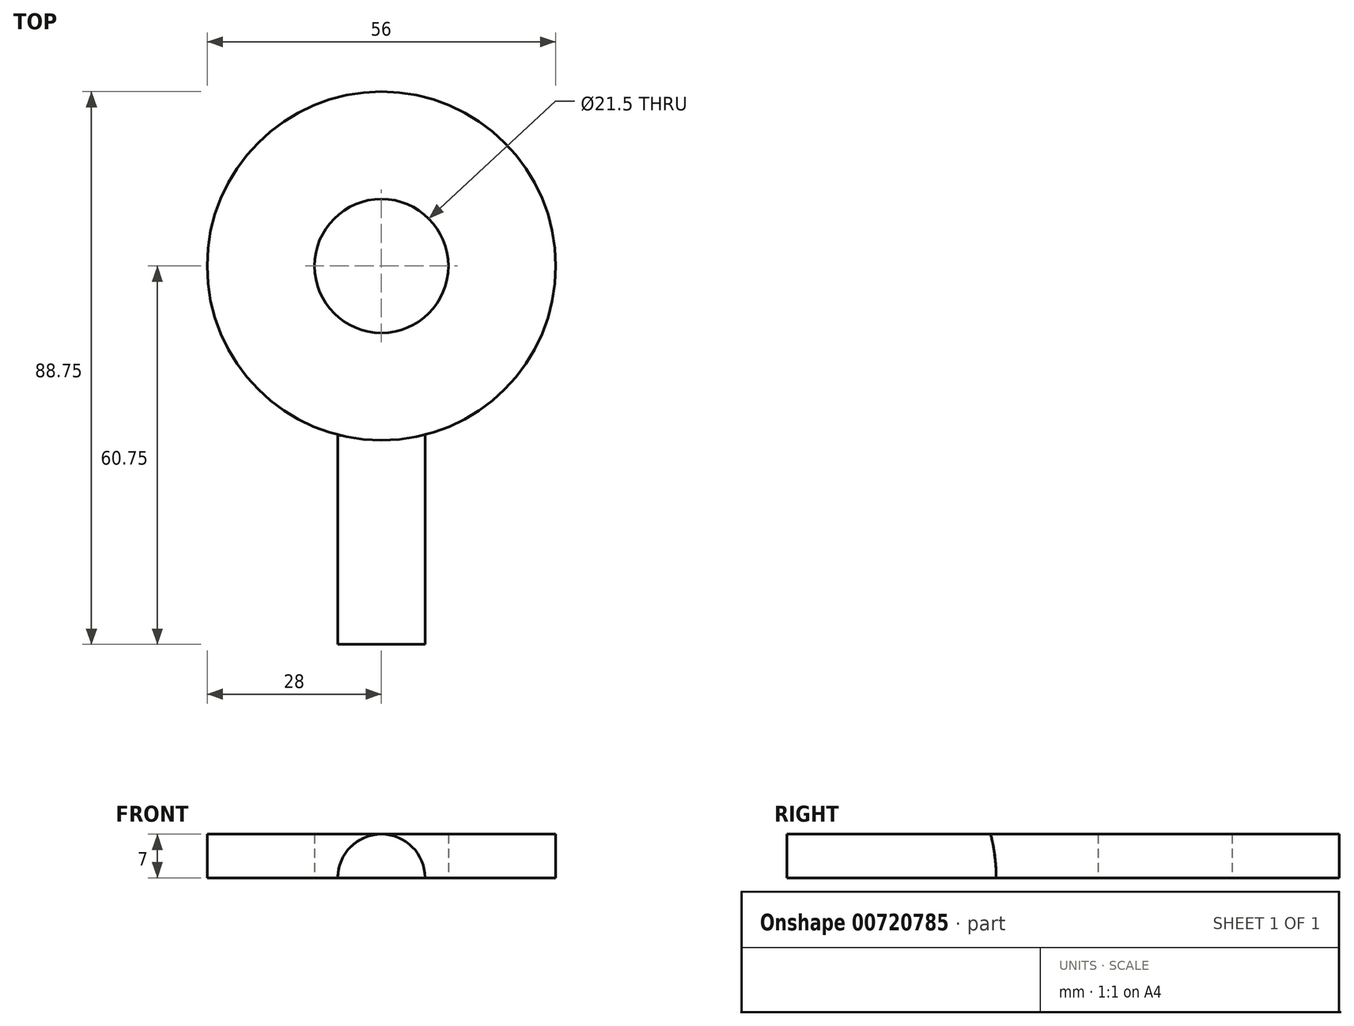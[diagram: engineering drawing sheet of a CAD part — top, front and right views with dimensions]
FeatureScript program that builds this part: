
annotation { "Feature Type Name" : "Feature", "Feature Type Description" : "" }
export const myFeature = defineFeature(function(context is Context, id is Id, definition is map)
    precondition{}
    {
        {
            var Q0;
            Q0=qCreatedBy(makeId("Front.planeOp"),FACE);
            var sketch = newSketch(context, id + "F0", { "sketchPlane" : qUnion([Q0])});
            skLineSegment(sketch, "E0", {"start": v(0, 0) * mm, "end": v(10, 0) * mm});
            skLineSegment(sketch, "E1", {"start": v(0, 0) * mm, "end": v(-2, 0) * mm});
            skLineSegment(sketch, "E2", {"start": v(10, 0) * mm, "end": v(12, 0) * mm});
            skArc(sketch, "E3", {"start": v(12, 0) * mm, "mid": v(5, 7) * mm, "end": v(-2, 0) * mm});
            skSolve(sketch);
        }
        {
            var Q0;
            {var subQ0=sQuery(id+"F0.wireOp",EDGE,"E0");Q0=makeQuery(id+"F0.imprint","IMPRINT",FACE,{"disambiguationData":[TD([[makeQuery(id+"F0.imprint","IMPRINT",EDGE,{"derivedFrom":subQ0}),1.0]])]});}
            extrude(context, id + "F1", {"entities" : qUnion([Q0]), "depth" : 50 * mm, "offsetDistance" : 25 * mm});
        }
        {
            var Q0;
            Q0=qCreatedBy(makeId("Top.planeOp"),FACE);
            var sketch = newSketch(context, id + "F2", { "sketchPlane" : qUnion([Q0])});
            skCircle(sketch, "E4", {"center": v(5, 10.75) * mm, "radius": 28 * mm});
            skCircle(sketch, "E5", {"center": v(5, 10.75) * mm, "radius": 10.75 * mm});
            skSolve(sketch);
        }
        {
            var Q0;
            Q0=makeQuery(id+"F2.imprint","IMPRINT",FACE,{"disambiguationData":[TD([[makeQuery(id+"F2.imprint","IMPRINT",EDGE,{"derivedFrom":sQuery(id+"F2.wireOp",EDGE,"E4")}),1.0]])]});
            extrude(context, id + "F3", {"entities" : qUnion([Q0]), "operationType" : NewBodyOperationType.ADD, "depth" : 7 * mm, "offsetDistance" : 25 * mm});
        }
    });
